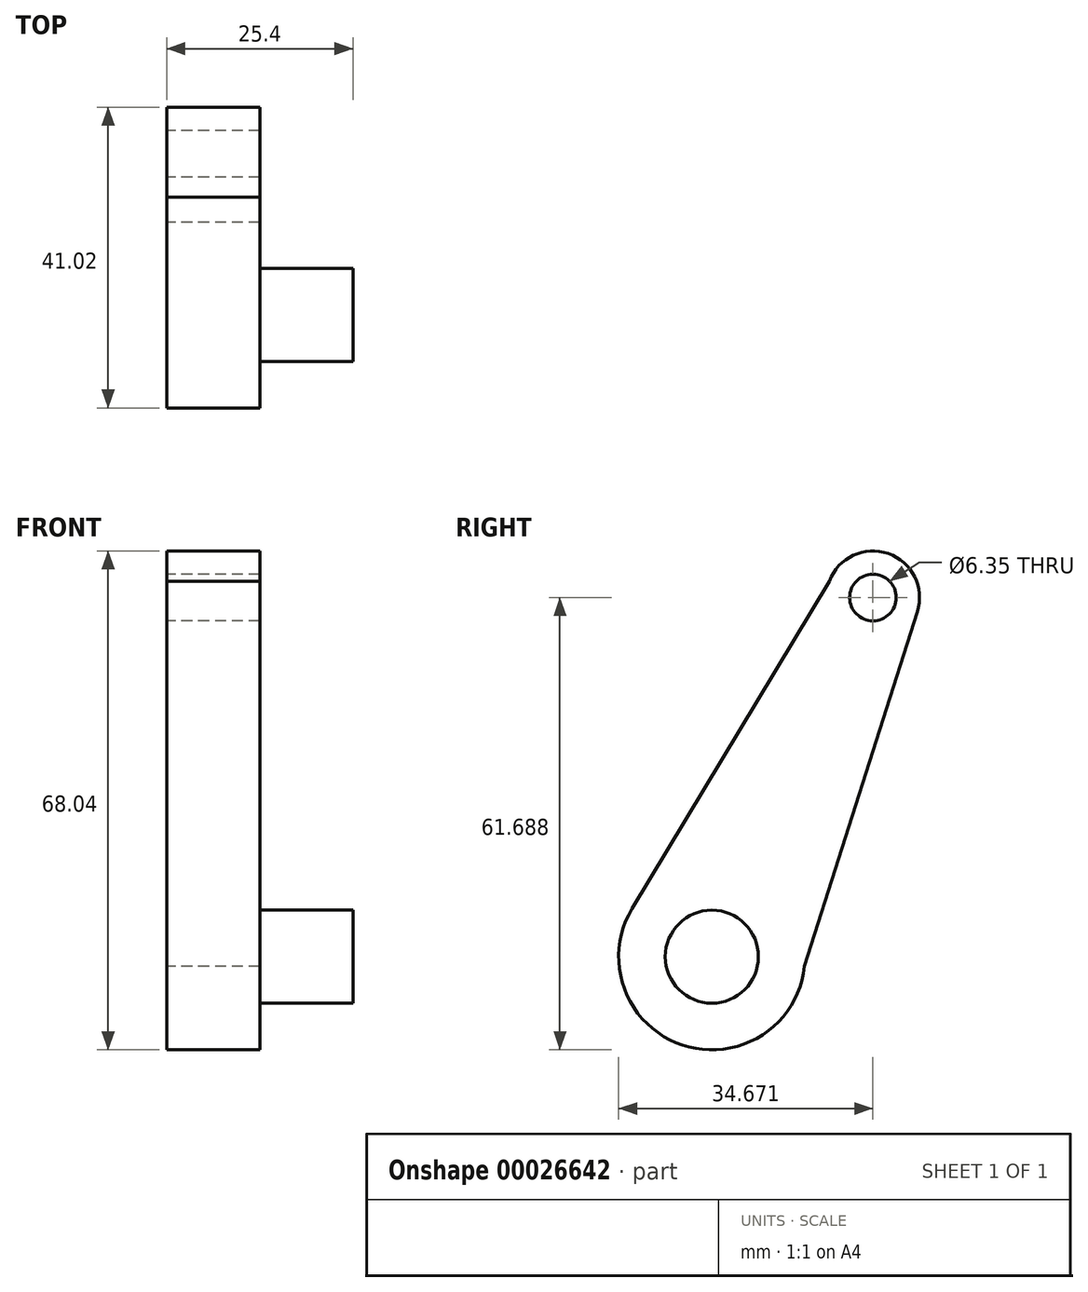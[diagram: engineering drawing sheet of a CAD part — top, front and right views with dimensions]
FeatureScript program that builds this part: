
annotation { "Feature Type Name" : "Feature", "Feature Type Description" : "" }
export const myFeature = defineFeature(function(context is Context, id is Id, definition is map)
    precondition{}
    {
        {
            var Q0;
            Q0=qCreatedBy(makeId("Right.planeOp"),FACE);
            var sketch = newSketch(context, id + "F0", { "sketchPlane" : qUnion([Q0])});
            skLineSegment(sketch, "E0", {"start": v(-26.91, -13.46) * mm, "end": v(0, 31.22) * mm});
            skLineSegment(sketch, "E1", {"start": v(12, 27.05) * mm, "end": v(-3.4, -21.3) * mm});
            skArc(sketch, "E2", {"start": v(-26.91, -13.46) * mm, "mid": v(-20.05, -32.06) * mm, "end": v(-3.4, -21.3) * mm});
            skCircle(sketch, "E3", {"center": v(-16.03, -20) * mm, "radius": 6.35 * mm});
            skArc(sketch, "E4", {"start": v(12, 27.05) * mm, "mid": v(8.03, 34.98) * mm, "end": v(0, 31.22) * mm});
            skCircle(sketch, "E5", {"center": v(5.94, 28.98) * mm, "radius": 3.18 * mm});
            skSolve(sketch);
        }
        {
            var Q0;
            Q0=makeQuery(id+"F0.imprint","IMPRINT",FACE,{"disambiguationData":[TD([[makeQuery(id+"F0.imprint","IMPRINT",EDGE,{"derivedFrom":sQuery(id+"F0.wireOp",EDGE,"E0")}),-1.0]])]});
            extrude(context, id + "F1", {"entities" : qUnion([Q0]), "depth" : 12.7 * mm});
        }
        {
            var Q0;
            Q0=makeQuery(id+"F0.imprint","IMPRINT",FACE,{"disambiguationData":[TD([[makeQuery(id+"F0.imprint","IMPRINT",EDGE,{"derivedFrom":sQuery(id+"F0.wireOp",EDGE,"E3")}),1.0]])]});
            extrude(context, id + "F2", {"entities" : qUnion([Q0]), "operationType" : NewBodyOperationType.ADD, "depth" : 25.4 * mm});
        }
    });
